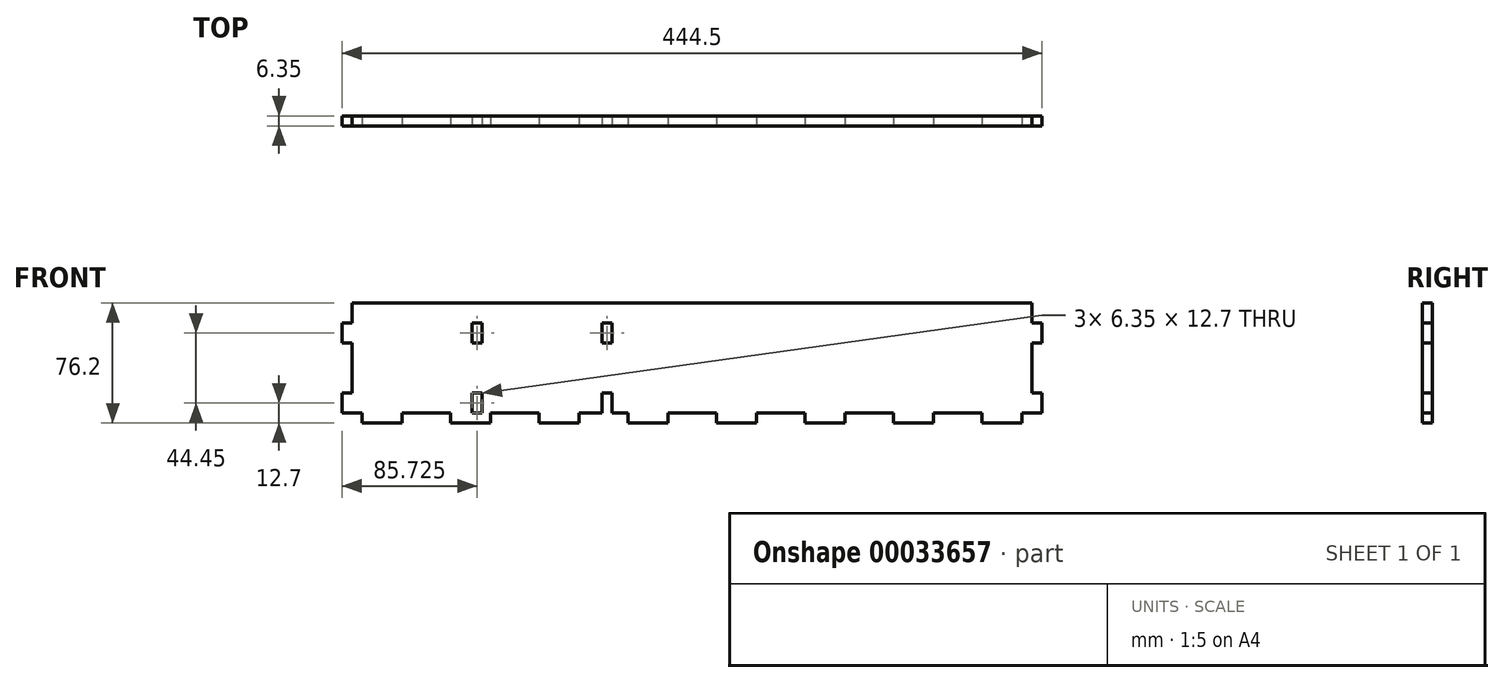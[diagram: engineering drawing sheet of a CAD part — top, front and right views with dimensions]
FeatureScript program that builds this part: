
annotation { "Feature Type Name" : "Feature", "Feature Type Description" : "" }
export const myFeature = defineFeature(function(context is Context, id is Id, definition is map)
    precondition{}
    {
        {
            var Q0;
            Q0=qCreatedBy(makeId("Front.planeOp"),FACE);
            var sketch = newSketch(context, id + "F0", { "sketchPlane" : qUnion([Q0])});
            skLineSegment(sketch, "E0.bottom", {"start": v(0, 0) * mm, "end": v(444.5, 0) * mm});
            skLineSegment(sketch, "E0.top", {"start": v(0, 76.2) * mm, "end": v(444.5, 76.2) * mm});
            skLineSegment(sketch, "E0.left", {"start": v(0, 0) * mm, "end": v(0, 76.2) * mm});
            skLineSegment(sketch, "E0.right", {"start": v(444.5, 0) * mm, "end": v(444.5, 76.2) * mm});
            skSolve(sketch);
        }
        {
            var Q0;
            Q0=makeQuery(id+"F0.imprint","IMPRINT",FACE,{"disambiguationData":[TD([[makeQuery(id+"F0.imprint","IMPRINT",EDGE,{"derivedFrom":sQuery(id+"F0.wireOp",EDGE,"E0.bottom")}),1.0]])]});
            extrude(context, id + "F1", {"entities" : qUnion([Q0]), "depth" : 6.35 * mm});
        }
        {
            var Q0;
            Q0=makeQuery(id+"F1.opExtrude","CAP_FACE",FACE,{"disambiguationData":[OSD([sQuery(id+"F0.wireOp",EDGE,"E0.bottom"),sQuery(id+"F0.wireOp",EDGE,"E0.top"),sQuery(id+"F0.wireOp",EDGE,"E0.left"),sQuery(id+"F0.wireOp",EDGE,"E0.right")])],"isStart":false});
            var sketch = newSketch(context, id + "F2", { "sketchPlane" : qUnion([Q0])});
            skLineSegment(sketch, "E1", {"start": v(222.25, 76.2) * mm, "end": v(222.25, 0) * mm, "construction": true});
            skLineSegment(sketch, "E2.bottom", {"start": v(0, 0) * mm, "end": v(6.35, 0) * mm});
            skLineSegment(sketch, "E2.top", {"start": v(0, 6.35) * mm, "end": v(6.35, 6.35) * mm});
            skLineSegment(sketch, "E2.left", {"start": v(0, 0) * mm, "end": v(0, 6.35) * mm});
            skLineSegment(sketch, "E2.right", {"start": v(6.35, 0) * mm, "end": v(6.35, 6.35) * mm});
            skLineSegment(sketch, "E3.bottom", {"start": v(0, 76.2) * mm, "end": v(6.35, 76.2) * mm});
            skLineSegment(sketch, "E3.top", {"start": v(0, 63.5) * mm, "end": v(6.35, 63.5) * mm});
            skLineSegment(sketch, "E3.left", {"start": v(0, 76.2) * mm, "end": v(0, 63.5) * mm});
            skLineSegment(sketch, "E3.right", {"start": v(6.35, 76.2) * mm, "end": v(6.35, 63.5) * mm});
            skLineSegment(sketch, "E4.bottom", {"start": v(0, 19.05) * mm, "end": v(6.35, 19.05) * mm});
            skLineSegment(sketch, "E4.top", {"start": v(0, 50.8) * mm, "end": v(6.35, 50.8) * mm});
            skLineSegment(sketch, "E4.left", {"start": v(0, 19.05) * mm, "end": v(0, 50.8) * mm});
            skLineSegment(sketch, "E4.right", {"start": v(6.35, 19.05) * mm, "end": v(6.35, 50.8) * mm});
            skLineSegment(sketch, "E5.MirrorCS", {"start": v(444.5, 6.35) * mm, "end": v(438.15, 6.35) * mm});
            skLineSegment(sketch, "E6.MirrorCS", {"start": v(444.5, 19.05) * mm, "end": v(438.15, 19.05) * mm});
            skLineSegment(sketch, "E7.MirrorCS", {"start": v(444.5, 50.8) * mm, "end": v(438.15, 50.8) * mm});
            skLineSegment(sketch, "E8.MirrorCS", {"start": v(444.5, 0) * mm, "end": v(438.15, 0) * mm});
            skLineSegment(sketch, "E9.MirrorCS", {"start": v(438.15, 76.2) * mm, "end": v(438.15, 63.5) * mm});
            skLineSegment(sketch, "E10.MirrorCS", {"start": v(438.15, 0) * mm, "end": v(438.15, 6.35) * mm});
            skLineSegment(sketch, "E11.MirrorCS", {"start": v(444.5, 0) * mm, "end": v(444.5, 6.35) * mm});
            skLineSegment(sketch, "E12.MirrorCS", {"start": v(444.5, 63.5) * mm, "end": v(438.15, 63.5) * mm});
            skLineSegment(sketch, "E13.MirrorCS", {"start": v(444.5, 76.2) * mm, "end": v(438.15, 76.2) * mm});
            skLineSegment(sketch, "E14.MirrorCS", {"start": v(444.5, 76.2) * mm, "end": v(444.5, 63.5) * mm});
            skLineSegment(sketch, "E15.MirrorCS", {"start": v(438.15, 19.05) * mm, "end": v(438.15, 50.8) * mm});
            skLineSegment(sketch, "E16.MirrorCS", {"start": v(444.5, 19.05) * mm, "end": v(444.5, 50.8) * mm});
            skSolve(sketch);
        }
        {
            var Q0;
            Q0=qSketchRegion(id+"F2",true);
            extrude(context, id + "F3", {"entities" : qUnion([Q0]), "operationType" : NewBodyOperationType.REMOVE, "endBound" : BoundingType.UP_TO_NEXT, "oppositeDirection" : true, "depth" : 25.4 * mm});
        }
        {
            var Q0;
            Q0=makeQuery(id+"F1.opExtrude","CAP_FACE",FACE,{"disambiguationData":[OSD([sQuery(id+"F0.wireOp",EDGE,"E0.bottom"),sQuery(id+"F0.wireOp",EDGE,"E0.top"),sQuery(id+"F0.wireOp",EDGE,"E0.left"),sQuery(id+"F0.wireOp",EDGE,"E0.right")])],"isStart":false});
            var sketch = newSketch(context, id + "F4", { "sketchPlane" : qUnion([Q0])});
            skLineSegment(sketch, "E17.bottom", {"start": v(38.1, 0) * mm, "end": v(68.94, 0) * mm});
            skLineSegment(sketch, "E17.top", {"start": v(38.1, 6.35) * mm, "end": v(68.94, 6.35) * mm});
            skLineSegment(sketch, "E17.left", {"start": v(38.1, 0) * mm, "end": v(38.1, 6.35) * mm});
            skLineSegment(sketch, "E17.right", {"start": v(68.94, 0) * mm, "end": v(68.94, 6.35) * mm});
            skLineSegment(sketch, "E18.1.0.0", {"start": v(125.19, 0) * mm, "end": v(125.19, 6.35) * mm});
            skLineSegment(sketch, "E18.1.0.1", {"start": v(94.34, 0) * mm, "end": v(94.34, 6.35) * mm});
            skLineSegment(sketch, "E18.1.0.2", {"start": v(94.34, 6.35) * mm, "end": v(125.19, 6.35) * mm});
            skLineSegment(sketch, "E18.1.0.3", {"start": v(94.34, 0) * mm, "end": v(125.19, 0) * mm});
            skLineSegment(sketch, "E18.2.0.0", {"start": v(181.43, 0) * mm, "end": v(181.43, 6.35) * mm});
            skLineSegment(sketch, "E18.2.0.1", {"start": v(150.59, 0) * mm, "end": v(150.59, 6.35) * mm});
            skLineSegment(sketch, "E18.2.0.2", {"start": v(150.59, 6.35) * mm, "end": v(181.43, 6.35) * mm});
            skLineSegment(sketch, "E18.2.0.3", {"start": v(150.59, 0) * mm, "end": v(181.43, 0) * mm});
            skLineSegment(sketch, "E18.3.0.0", {"start": v(237.67, 0) * mm, "end": v(237.67, 6.35) * mm});
            skLineSegment(sketch, "E18.3.0.1", {"start": v(206.83, 0) * mm, "end": v(206.83, 6.35) * mm});
            skLineSegment(sketch, "E18.3.0.2", {"start": v(206.83, 6.35) * mm, "end": v(237.67, 6.35) * mm});
            skLineSegment(sketch, "E18.3.0.3", {"start": v(206.83, 0) * mm, "end": v(237.67, 0) * mm});
            skLineSegment(sketch, "E18.4.0.0", {"start": v(293.91, 0) * mm, "end": v(293.91, 6.35) * mm});
            skLineSegment(sketch, "E18.4.0.1", {"start": v(263.07, 0) * mm, "end": v(263.07, 6.35) * mm});
            skLineSegment(sketch, "E18.4.0.2", {"start": v(263.07, 6.35) * mm, "end": v(293.91, 6.35) * mm});
            skLineSegment(sketch, "E18.4.0.3", {"start": v(263.07, 0) * mm, "end": v(293.91, 0) * mm});
            skLineSegment(sketch, "E18.direction1", {"start": v(68.94, 0) * mm, "end": v(125.19, 0) * mm, "construction": true});
            skLineSegment(sketch, "E19.0.5.0", {"start": v(350.16, 0) * mm, "end": v(350.16, 6.35) * mm});
            skLineSegment(sketch, "E19.3.5.0", {"start": v(319.31, 0) * mm, "end": v(319.31, 6.35) * mm});
            skLineSegment(sketch, "E19.6.5.0", {"start": v(319.31, 6.35) * mm, "end": v(350.16, 6.35) * mm});
            skLineSegment(sketch, "E19.9.5.0", {"start": v(319.31, 0) * mm, "end": v(350.16, 0) * mm});
            skLineSegment(sketch, "E19.0.6.0", {"start": v(406.4, 0) * mm, "end": v(406.4, 6.35) * mm});
            skLineSegment(sketch, "E19.3.6.0", {"start": v(375.56, 0) * mm, "end": v(375.56, 6.35) * mm});
            skLineSegment(sketch, "E19.6.6.0", {"start": v(375.56, 6.35) * mm, "end": v(406.4, 6.35) * mm});
            skLineSegment(sketch, "E19.9.6.0", {"start": v(375.56, 0) * mm, "end": v(406.4, 0) * mm});
            skLineSegment(sketch, "E20.bottom", {"start": v(6.35, 6.35) * mm, "end": v(12.7, 6.35) * mm});
            skLineSegment(sketch, "E20.top", {"start": v(6.35, 0) * mm, "end": v(12.7, 0) * mm});
            skLineSegment(sketch, "E20.left", {"start": v(6.35, 6.35) * mm, "end": v(6.35, 0) * mm});
            skLineSegment(sketch, "E20.right", {"start": v(12.7, 6.35) * mm, "end": v(12.7, 0) * mm});
            skLineSegment(sketch, "E21.bottom", {"start": v(438.15, 6.35) * mm, "end": v(431.8, 6.35) * mm});
            skLineSegment(sketch, "E21.top", {"start": v(438.15, 0) * mm, "end": v(431.8, 0) * mm});
            skLineSegment(sketch, "E21.left", {"start": v(438.15, 6.35) * mm, "end": v(438.15, 0) * mm});
            skLineSegment(sketch, "E21.right", {"start": v(431.8, 6.35) * mm, "end": v(431.8, 0) * mm});
            skSolve(sketch);
        }
        {
            var Q0;
            Q0=qSketchRegion(id+"F4",true);
            extrude(context, id + "F5", {"entities" : qUnion([Q0]), "operationType" : NewBodyOperationType.REMOVE, "endBound" : BoundingType.THROUGH_ALL, "oppositeDirection" : true, "depth" : 25.4 * mm});
        }
        {
            var Q0;
            Q0=makeQuery(id+"F1.opExtrude","CAP_FACE",FACE,{"disambiguationData":[OSD([sQuery(id+"F0.wireOp",EDGE,"E0.bottom"),sQuery(id+"F0.wireOp",EDGE,"E0.top"),sQuery(id+"F0.wireOp",EDGE,"E0.left"),sQuery(id+"F0.wireOp",EDGE,"E0.right")])],"isStart":false});
            var sketch = newSketch(context, id + "F6", { "sketchPlane" : qUnion([Q0])});
            skLineSegment(sketch, "E22.bottom", {"start": v(82.55, 19.05) * mm, "end": v(88.9, 19.05) * mm});
            skLineSegment(sketch, "E22.top", {"start": v(82.55, 6.35) * mm, "end": v(88.9, 6.35) * mm});
            skLineSegment(sketch, "E22.left", {"start": v(82.55, 19.05) * mm, "end": v(82.55, 6.35) * mm});
            skLineSegment(sketch, "E22.right", {"start": v(88.9, 19.05) * mm, "end": v(88.9, 6.35) * mm});
            skLineSegment(sketch, "E23.bottom", {"start": v(82.55, 50.8) * mm, "end": v(88.9, 50.8) * mm});
            skLineSegment(sketch, "E23.top", {"start": v(82.55, 63.5) * mm, "end": v(88.9, 63.5) * mm});
            skLineSegment(sketch, "E23.left", {"start": v(82.55, 50.8) * mm, "end": v(82.55, 63.5) * mm});
            skLineSegment(sketch, "E23.right", {"start": v(88.9, 50.8) * mm, "end": v(88.9, 63.5) * mm});
            skLineSegment(sketch, "E24.1.0.0", {"start": v(165.1, 19.05) * mm, "end": v(165.1, 6.35) * mm});
            skLineSegment(sketch, "E24.1.0.1", {"start": v(165.1, 6.35) * mm, "end": v(171.45, 6.35) * mm});
            skLineSegment(sketch, "E24.1.0.2", {"start": v(165.1, 19.05) * mm, "end": v(171.45, 19.05) * mm});
            skLineSegment(sketch, "E24.1.0.3", {"start": v(171.45, 19.05) * mm, "end": v(171.45, 6.35) * mm});
            skLineSegment(sketch, "E24.1.0.4", {"start": v(165.1, 50.8) * mm, "end": v(171.45, 50.8) * mm});
            skLineSegment(sketch, "E24.1.0.5", {"start": v(165.1, 63.5) * mm, "end": v(171.45, 63.5) * mm});
            skLineSegment(sketch, "E24.1.0.6", {"start": v(165.1, 50.8) * mm, "end": v(165.1, 63.5) * mm});
            skLineSegment(sketch, "E24.1.0.7", {"start": v(171.45, 50.8) * mm, "end": v(171.45, 63.5) * mm});
            skLineSegment(sketch, "E24.direction1", {"start": v(82.55, 6.35) * mm, "end": v(165.1, 6.35) * mm, "construction": true});
            skSolve(sketch);
        }
        {
            var Q0;
            Q0 = qSketchRegion(id + "F6", true);
            extrude(context, id + "F7", {"entities" : qUnion([Q0]), "operationType" : NewBodyOperationType.REMOVE, "endBound" : BoundingType.THROUGH_ALL, "oppositeDirection" : true, "depth" : 25.4 * mm});
        }
    });
